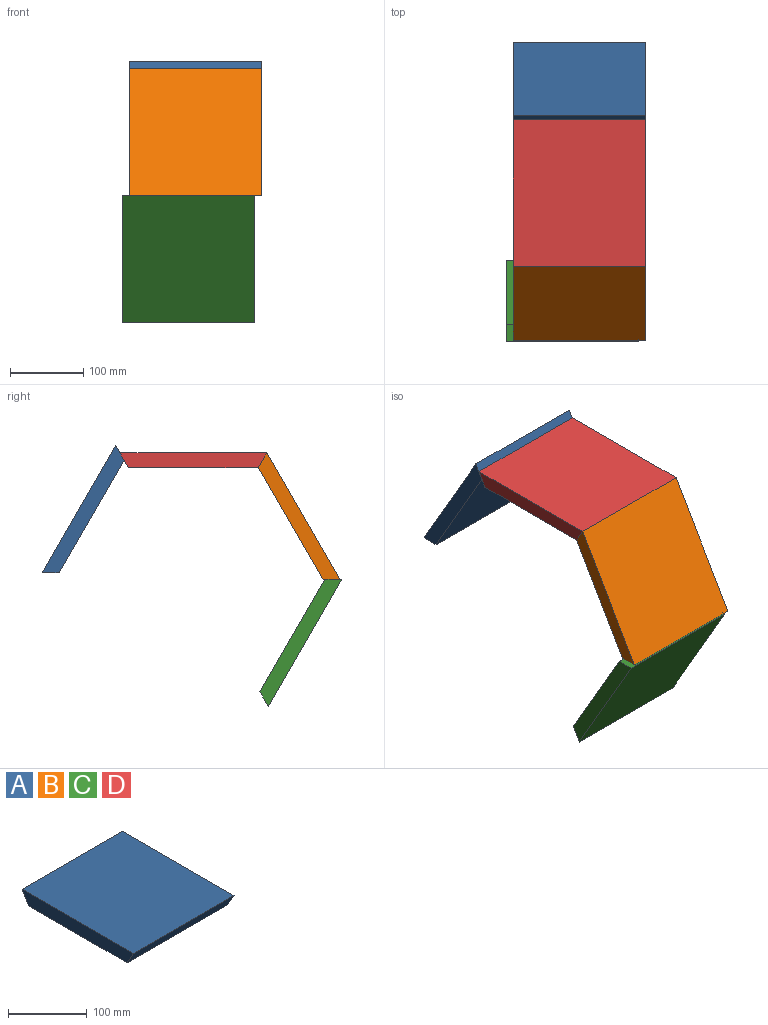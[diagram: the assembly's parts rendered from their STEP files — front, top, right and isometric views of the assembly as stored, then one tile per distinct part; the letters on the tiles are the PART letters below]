
ASSEMBLY  parts=4 mates=2
PART A: 6 faces, bbox 180x200x20 mm
  f0: plane 200x180mm, normal (0,0,1), area 36000mm2, adj f1,f3,f4,f5
  f1: plane 180x20mm, normal (0,-0.87,-0.5), area 4156.9mm2, adj f0,f2,f4,f5
  f2: plane 180x176.91mm, normal (0,0,-1), area 31843.1mm2, adj f1,f3,f4,f5
  f3: plane 180x20mm, normal (0,0.87,-0.5), area 4156.9mm2, adj f0,f2,f4,f5
  f4: plane 200x20mm, normal (1,0,0), area 3769.1mm2, adj f0,f1,f2,f3
  f5: plane 200x20mm, normal (-1,0,0), area 3769.1mm2, adj f0,f1,f2,f3
PART B: same geometry as A
PART C: same geometry as A
PART D: same geometry as A
PLACE A rot(axis=(-1,0,0),60deg) t=(-33.7,197.79,-1.35)mm
PLACE B rot(axis=(1,0,0),60deg) t=(-33.7,-107.98,-184.55)mm
PLACE C rot(axis=(1,0,0),120deg) t=(-42.63,-10.23,-356.95)mm
PLACE D rot(axis=(0.06,0.04,-1),0deg) t=(-33.7,-7.98,-11.35)mm
MATE fastened B.f3 <-> D.f1  axis (0,0.87,0.5) through (56.3,-2.21,-21.35)mm
MATE fastened A.f1 <-> D.f3  axis (0,-0.87,0.5) through (56.3,192.02,-11.35)mm
